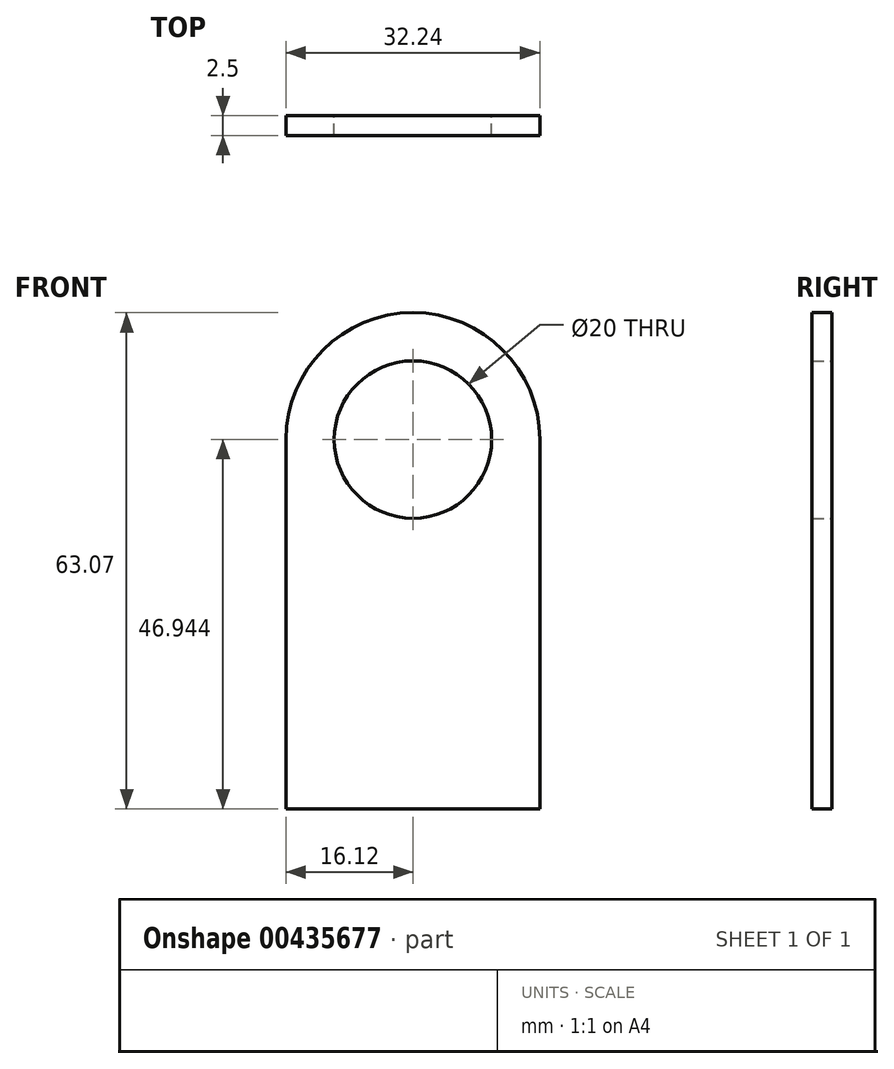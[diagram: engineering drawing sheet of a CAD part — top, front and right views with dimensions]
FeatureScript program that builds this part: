
annotation { "Feature Type Name" : "Feature", "Feature Type Description" : "" }
export const myFeature = defineFeature(function(context is Context, id is Id, definition is map)
    precondition{}
    {
        {
            var Q0;
            Q0=qCreatedBy(makeId("Front.planeOp"),FACE);
            var sketch = newSketch(context, id + "F0", { "sketchPlane" : qUnion([Q0])});
            skLineSegment(sketch, "E0", {"start": v(0, 0) * mm, "end": v(0, 46.94) * mm});
            skArc(sketch, "E1.0.endCap", {"start": v(-16.12, 46.94) * mm, "mid": v(0, 63.07) * mm, "end": v(16.12, 46.94) * mm});
            skLineSegment(sketch, "E1.0.left", {"start": v(-16.12, 0) * mm, "end": v(-16.12, 46.94) * mm});
            skLineSegment(sketch, "E1.0.right", {"start": v(16.12, 0) * mm, "end": v(16.12, 46.94) * mm});
            skLineSegment(sketch, "E2", {"start": v(16.12, 0) * mm, "end": v(-16.12, 0) * mm});
            skCircle(sketch, "E3", {"center": v(0, 46.94) * mm, "radius": 10 * mm});
            skSolve(sketch);
        }
        {
            var Q0;
            Q0 = qSketchRegion(id + "F0", true);
            extrude(context, id + "F1", {"entities" : qUnion([Q0]), "depth" : 2.5 * mm});
        }
    });
